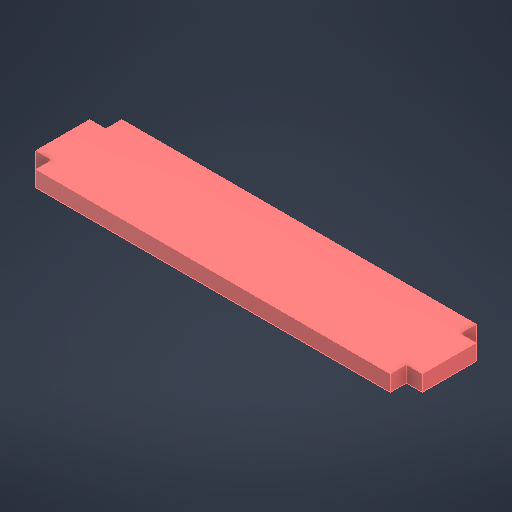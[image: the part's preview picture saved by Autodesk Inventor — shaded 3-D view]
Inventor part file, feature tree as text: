
AUTODESK INVENTOR PART (.ipt)
format: ipt  version: 2025.3 (Build 293356030, 356C)  size: 190,464 bytes
history: native  units: mm
features: other x1, extrude x1, sketch x1
ambient origin geometry x8: Origin, YZ Plane, XZ Plane, XY Plane, X Axis, Y Axis, Z Axis, Center Point
bodies: Body1 (feature_tree)
feature tree (3):
  other  "實體1"
  extrude  "擠出1"  Depth=66.0mm
  sketch  "草圖1"
